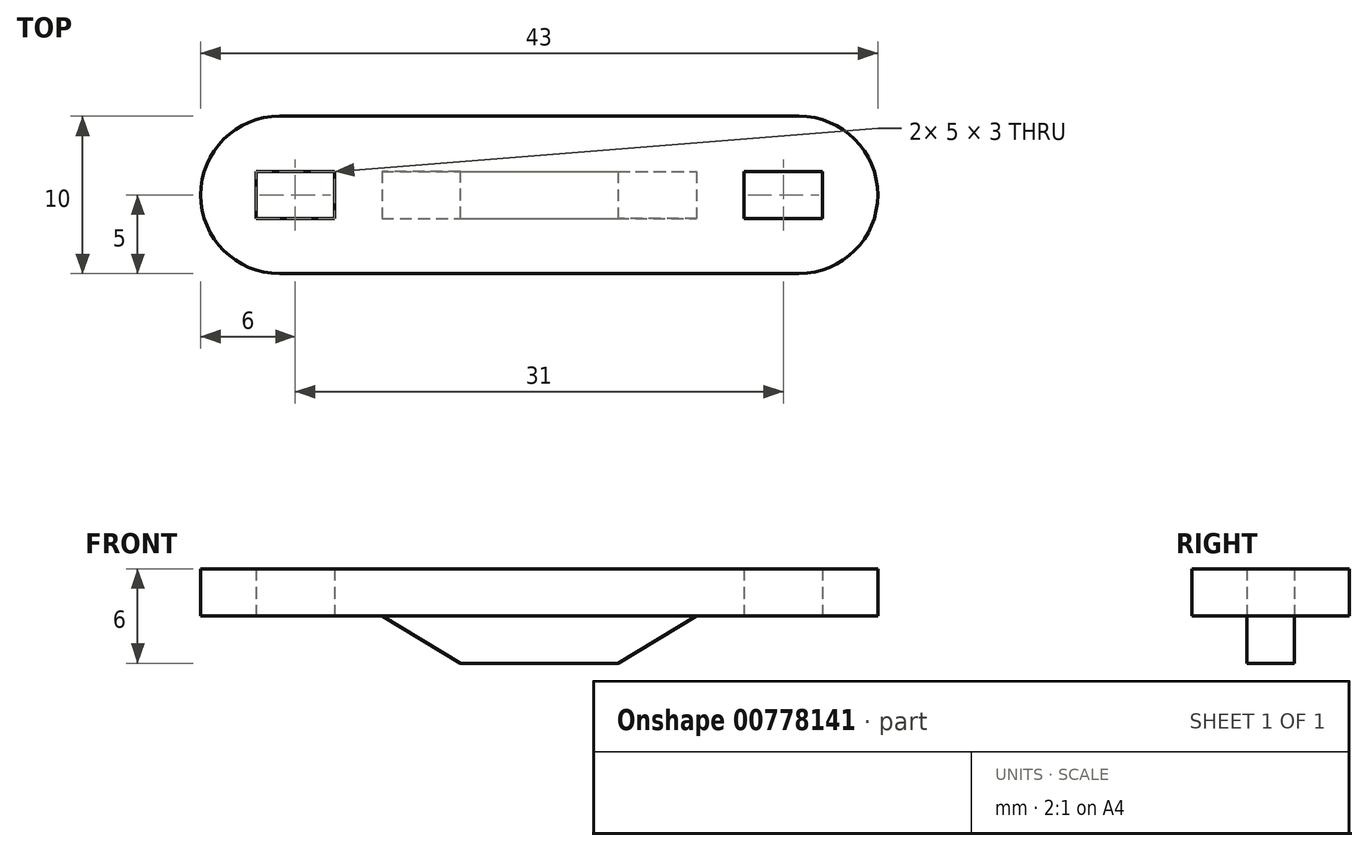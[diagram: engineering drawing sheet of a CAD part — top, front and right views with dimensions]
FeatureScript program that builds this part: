
annotation { "Feature Type Name" : "Feature", "Feature Type Description" : "" }
export const myFeature = defineFeature(function(context is Context, id is Id, definition is map)
    precondition{}
    {
        {
            var Q0;
            Q0=qCreatedBy(makeId("Top.planeOp"),FACE);
            var sketch = newSketch(context, id + "F0", { "sketchPlane" : qUnion([Q0])});
            skLineSegment(sketch, "E0.bottom", {"start": v(-16.5, 10) * mm, "end": v(16.5, 10) * mm});
            skLineSegment(sketch, "E0.top", {"start": v(-16.5, 0) * mm, "end": v(16.5, 0) * mm});
            skLineSegment(sketch, "E0.left", {"start": v(-21.5, 5) * mm, "end": v(-21.5, 5) * mm});
            skLineSegment(sketch, "E0.right", {"start": v(21.5, 5) * mm, "end": v(21.5, 5) * mm});
            skPoint(sketch, "E1.visualSharp", {"position": v(21.5, 10) * mm});
            skArc(sketch, "E1.filletArc", {"start": v(21.5, 5) * mm, "mid": v(20.04, 8.54) * mm, "end": v(16.5, 10) * mm});
            skPoint(sketch, "E2.visualSharp", {"position": v(-21.5, 10) * mm});
            skArc(sketch, "E2.filletArc", {"start": v(-16.5, 10) * mm, "mid": v(-20.04, 8.54) * mm, "end": v(-21.5, 5) * mm});
            skLineSegment(sketch, "E3.bottom", {"start": v(-18, 6.5) * mm, "end": v(-13, 6.5) * mm});
            skLineSegment(sketch, "E3.top", {"start": v(-18, 3.5) * mm, "end": v(-13, 3.5) * mm});
            skLineSegment(sketch, "E3.left", {"start": v(-18, 6.5) * mm, "end": v(-18, 3.5) * mm});
            skLineSegment(sketch, "E3.right", {"start": v(-13, 6.5) * mm, "end": v(-13, 3.5) * mm});
            skLineSegment(sketch, "E4.MirrorCS", {"start": v(13, 6.5) * mm, "end": v(13, 3.5) * mm});
            skLineSegment(sketch, "E5.MirrorCS", {"start": v(18, 6.5) * mm, "end": v(18, 3.5) * mm});
            skLineSegment(sketch, "E6.MirrorCS", {"start": v(18, 6.5) * mm, "end": v(13, 6.5) * mm});
            skLineSegment(sketch, "E7.MirrorCS", {"start": v(18, 3.5) * mm, "end": v(13, 3.5) * mm});
            skPoint(sketch, "E8.visualSharp", {"position": v(-21.5, 0) * mm});
            skArc(sketch, "E8.filletArc", {"start": v(-21.5, 5) * mm, "mid": v(-20.04, 1.46) * mm, "end": v(-16.5, 0) * mm});
            skPoint(sketch, "E9.visualSharp", {"position": v(21.5, 0) * mm});
            skArc(sketch, "E9.filletArc", {"start": v(16.5, 0) * mm, "mid": v(20.04, 1.46) * mm, "end": v(21.5, 5) * mm});
            skLineSegment(sketch, "E10.bottom", {"start": v(-10, 6.5) * mm, "end": v(10, 6.5) * mm});
            skLineSegment(sketch, "E10.top", {"start": v(-10, 3.5) * mm, "end": v(10, 3.5) * mm});
            skLineSegment(sketch, "E10.left", {"start": v(-10, 6.5) * mm, "end": v(-10, 3.5) * mm});
            skLineSegment(sketch, "E10.right", {"start": v(10, 6.5) * mm, "end": v(10, 3.5) * mm});
            skSolve(sketch);
        }
        {
            var Q0;
            Q0=makeQuery(id+"F0.imprint","IMPRINT",FACE,{"disambiguationData":[TD([[makeQuery(id+"F0.imprint","IMPRINT",EDGE,{"derivedFrom":sQuery(id+"F0.wireOp",EDGE,"E0.bottom")}),-1.0]])]});
            var Q1;
            Q1=makeQuery(id+"F0.imprint","IMPRINT",FACE,{"disambiguationData":[TD([[makeQuery(id+"F0.imprint","IMPRINT",EDGE,{"derivedFrom":sQuery(id+"F0.wireOp",EDGE,"E10.bottom")}),-1.0]])]});
            extrude(context, id + "F1", {"entities" : qUnion([Q0, Q1]), "depth" : 3 * mm, "offsetDistance" : 25 * mm});
        }
        {
            var Q0;
            Q0=makeQuery(id+"F0.imprint","IMPRINT",FACE,{"disambiguationData":[TD([[makeQuery(id+"F0.imprint","IMPRINT",EDGE,{"derivedFrom":sQuery(id+"F0.wireOp",EDGE,"E10.bottom")}),-1.0]])]});
            extrude(context, id + "F2", {"entities" : qUnion([Q0]), "operationType" : NewBodyOperationType.ADD, "oppositeDirection" : true, "depth" : 3 * mm, "offsetDistance" : 25 * mm});
        }
        {
            var Q0;
            Q0=makeQuery(id+"F2.opExtrude","CAP_EDGE",EDGE,{"disambiguationData":[OSD([sQuery(id+"F0.wireOp",EDGE,"E10.left")])],"isStart":false});
            var Q1;
            Q1=makeQuery(id+"F2.opExtrude","CAP_EDGE",EDGE,{"disambiguationData":[OSD([sQuery(id+"F0.wireOp",EDGE,"E10.right")])],"isStart":false});
            chamfer(context, id + "F3", {"entities" : qUnion([Q0, Q1]), "chamferType" : ChamferType.TWO_OFFSETS, "width1" : 3 * mm, "oppositeDirection" : false, "width2" : 5 * mm, "tangentPropagation" : true});
        }
    });
